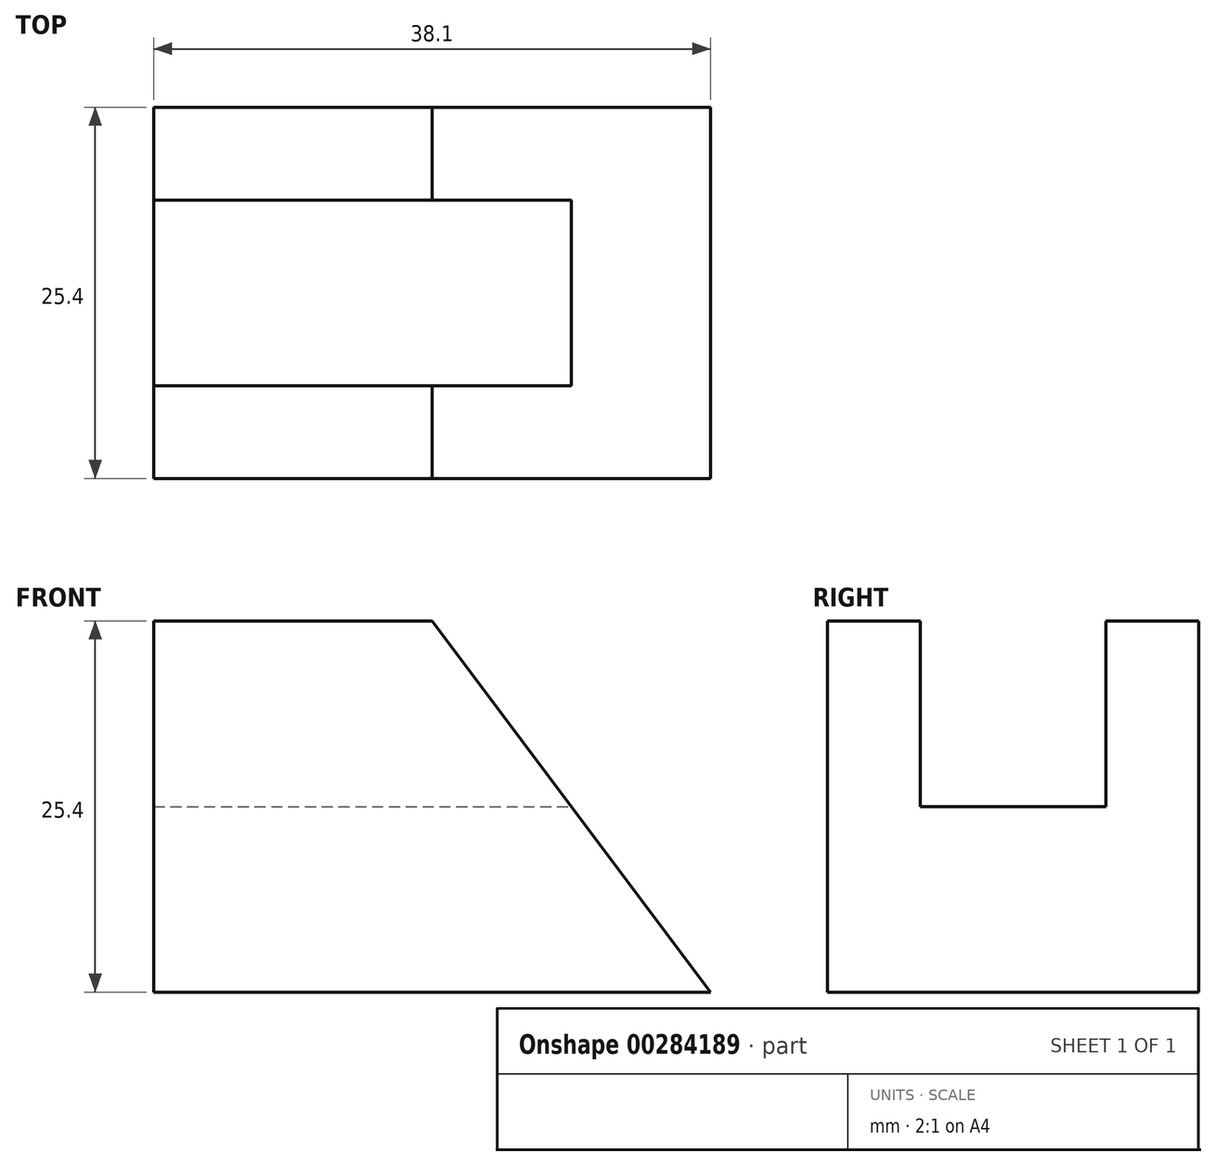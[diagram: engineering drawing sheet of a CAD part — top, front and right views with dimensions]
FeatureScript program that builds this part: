
annotation { "Feature Type Name" : "Feature", "Feature Type Description" : "" }
export const myFeature = defineFeature(function(context is Context, id is Id, definition is map)
    precondition{}
    {
        {
            var Q0;
            Q0=qCreatedBy(makeId("Front.planeOp"),FACE);
            var sketch = newSketch(context, id + "F0", { "sketchPlane" : qUnion([Q0])});
            skLineSegment(sketch, "E0", {"start": v(0, 0) * mm, "end": v(0, 25.4) * mm});
            skLineSegment(sketch, "E1", {"start": v(0, 25.4) * mm, "end": v(19.05, 25.4) * mm});
            skLineSegment(sketch, "E2", {"start": v(19.05, 25.4) * mm, "end": v(38.1, 0) * mm});
            skLineSegment(sketch, "E3", {"start": v(38.1, 0) * mm, "end": v(0, 0) * mm});
            skSolve(sketch);
        }
        {
            var Q0;
            Q0 = qSketchRegion(id + "F0", true);
            extrude(context, id + "F1", {"entities" : qUnion([Q0]), "depth" : 25.4 * mm});
        }
        {
            var Q0;
            Q0=makeQuery(id+"F1.opExtrude","SWEPT_FACE",FACE,{"disambiguationData":[OSD([sQuery(id+"F0.wireOp",EDGE,"E1")])]});
            var sketch = newSketch(context, id + "F2", { "sketchPlane" : qUnion([Q0])});
            skLineSegment(sketch, "E4.bottom", {"start": v(0, -6.35) * mm, "end": v(28.58, -6.35) * mm});
            skLineSegment(sketch, "E4.top", {"start": v(0, -19.05) * mm, "end": v(28.58, -19.05) * mm});
            skLineSegment(sketch, "E4.left", {"start": v(0, -6.35) * mm, "end": v(0, -19.05) * mm});
            skLineSegment(sketch, "E4.right", {"start": v(28.58, -6.35) * mm, "end": v(28.58, -19.05) * mm});
            skSolve(sketch);
        }
        {
            var Q0;
            {var subQ0=sQuery(id+"F2.wireOp",EDGE,"E4.left");Q0=makeQuery(id+"F2.imprint","IMPRINT",FACE,{"disambiguationData":[TD([[makeQuery(id+"F2.imprint","IMPRINT",EDGE,{"derivedFrom":subQ0}),-1.0]])]});}
            var Q1;
            {var subQ0=sQuery(id+"F2.wireOp",EDGE,"E4.right");Q1=makeQuery(id+"F2.imprint","IMPRINT",FACE,{"disambiguationData":[TD([[makeQuery(id+"F2.imprint","IMPRINT",EDGE,{"derivedFrom":subQ0}),-1.0]])]});}
            extrude(context, id + "F3", {"entities" : qUnion([Q0, Q1]), "operationType" : NewBodyOperationType.REMOVE, "oppositeDirection" : true, "depth" : 12.7 * mm});
        }
    });
